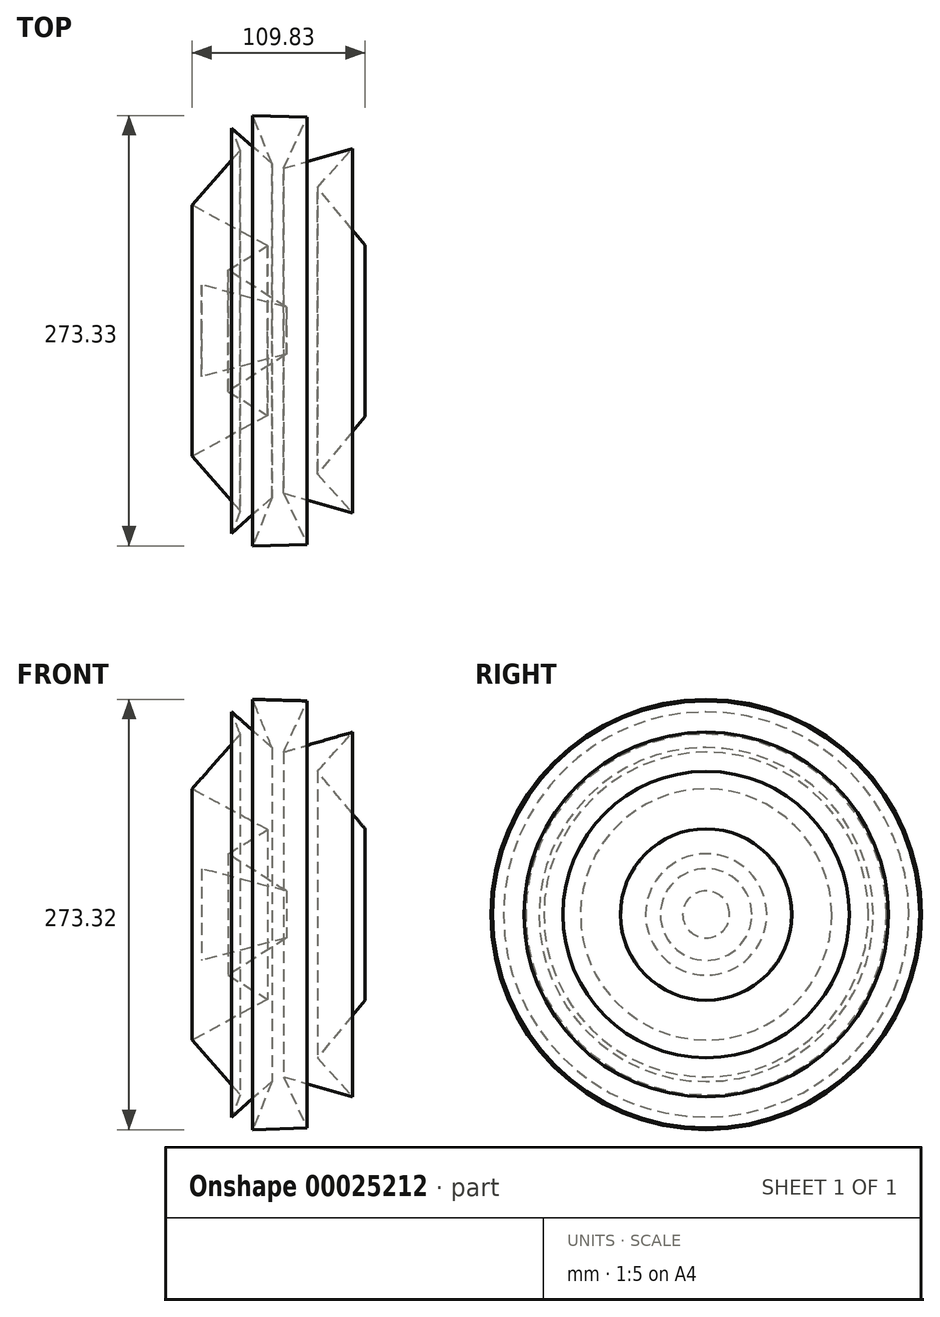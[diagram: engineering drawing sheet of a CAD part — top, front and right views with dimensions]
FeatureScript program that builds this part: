
annotation { "Feature Type Name" : "Feature", "Feature Type Description" : "" }
export const myFeature = defineFeature(function(context is Context, id is Id, definition is map)
    precondition{}
    {
        {
            var Q0;
            Q0=qCreatedBy(makeId("Top.planeOp"),FACE);
            var sketch = newSketch(context, id + "F0", { "sketchPlane" : qUnion([Q0])});
            skLineSegment(sketch, "E0", {"start": v(-27.46, 47.21) * mm, "end": v(-58.02, 12.42) * mm});
            skLineSegment(sketch, "E1", {"start": v(-58.02, 12.42) * mm, "end": v(-10.06, -13.42) * mm});
            skLineSegment(sketch, "E2", {"start": v(-10.06, -13.42) * mm, "end": v(-35.16, -28.82) * mm});
            skLineSegment(sketch, "E3", {"start": v(-52.06, -38.27) * mm, "end": v(1.86, -52.43) * mm});
            skLineSegment(sketch, "E4", {"start": v(1.86, -52.43) * mm, "end": v(-35.16, -28.82) * mm});
            skLineSegment(sketch, "E5", {"start": v(-52.06, -67.34) * mm, "end": v(-52.06, -38.27) * mm});
            skLineSegment(sketch, "E6", {"start": v(-52.06, -67.34) * mm, "end": v(51.8, -67.34) * mm});
            skLineSegment(sketch, "E7", {"start": v(51.8, -67.34) * mm, "end": v(51.8, -12.92) * mm});
            skLineSegment(sketch, "E8", {"start": v(51.8, -12.92) * mm, "end": v(21.5, 23.6) * mm});
            skLineSegment(sketch, "E9", {"start": v(21.5, 23.6) * mm, "end": v(43.86, 48.45) * mm});
            skLineSegment(sketch, "E10", {"start": v(43.86, 48.45) * mm, "end": v(0, 35.78) * mm});
            skLineSegment(sketch, "E11", {"start": v(0, 35.78) * mm, "end": v(15.03, 68.33) * mm});
            skLineSegment(sketch, "E12", {"start": v(15.03, 68.33) * mm, "end": v(-19.5, 69.33) * mm});
            skLineSegment(sketch, "E13", {"start": v(-19.5, 69.33) * mm, "end": v(-7.33, 38.76) * mm});
            skLineSegment(sketch, "E14", {"start": v(-7.33, 38.76) * mm, "end": v(-32.92, 61.37) * mm});
            skLineSegment(sketch, "E15", {"start": v(-32.92, 61.37) * mm, "end": v(-27.46, 47.21) * mm});
            skSolve(sketch);
        }
        {
            var Q0;
            Q0=makeQuery(id+"F0.imprint","IMPRINT",FACE,{"disambiguationData":[TD([[makeQuery(id+"F0.imprint","IMPRINT",EDGE,{"derivedFrom":sQuery(id+"F0.wireOp",EDGE,"E0")}),1.0]])]});
            var Q1;
            Q1=sQuery(id+"F0.wireOp",EDGE,"E6");
            revolve(context, id + "F1", {"entities" : qUnion([Q0]), "axis" : qUnion([Q1]), "revolveType" : RevolveType.FULL});
        }
    });
